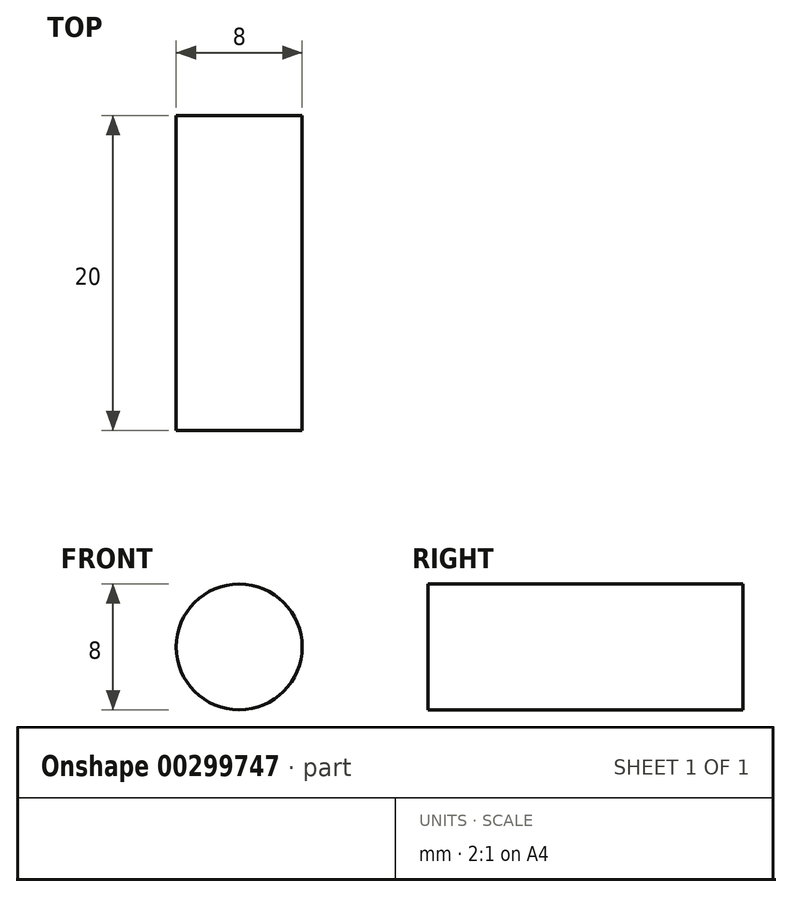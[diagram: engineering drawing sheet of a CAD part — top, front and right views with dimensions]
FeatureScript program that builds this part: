
annotation { "Feature Type Name" : "Feature", "Feature Type Description" : "" }
export const myFeature = defineFeature(function(context is Context, id is Id, definition is map)
    precondition{}
    {
        {
            var Q0;
            Q0=qCreatedBy(makeId("Front.planeOp"),FACE);
            var sketch = newSketch(context, id + "F0", { "sketchPlane" : qUnion([Q0])});
            skCircle(sketch, "E0", {"center": v(0, 0) * mm, "radius": 4 * mm});
            skSolve(sketch);
        }
        {
            var Q0;
            Q0=makeQuery(id+"F0.imprint","IMPRINT",FACE,{"disambiguationData":[TD([[makeQuery(id+"F0.imprint","IMPRINT",EDGE,{"derivedFrom":sQuery(id+"F0.wireOp",EDGE,"E0")}),1.0]])]});
            extrude(context, id + "F1", {"entities" : qUnion([Q0]), "depth" : 20 * mm, "symmetric" : true});
        }
    });
